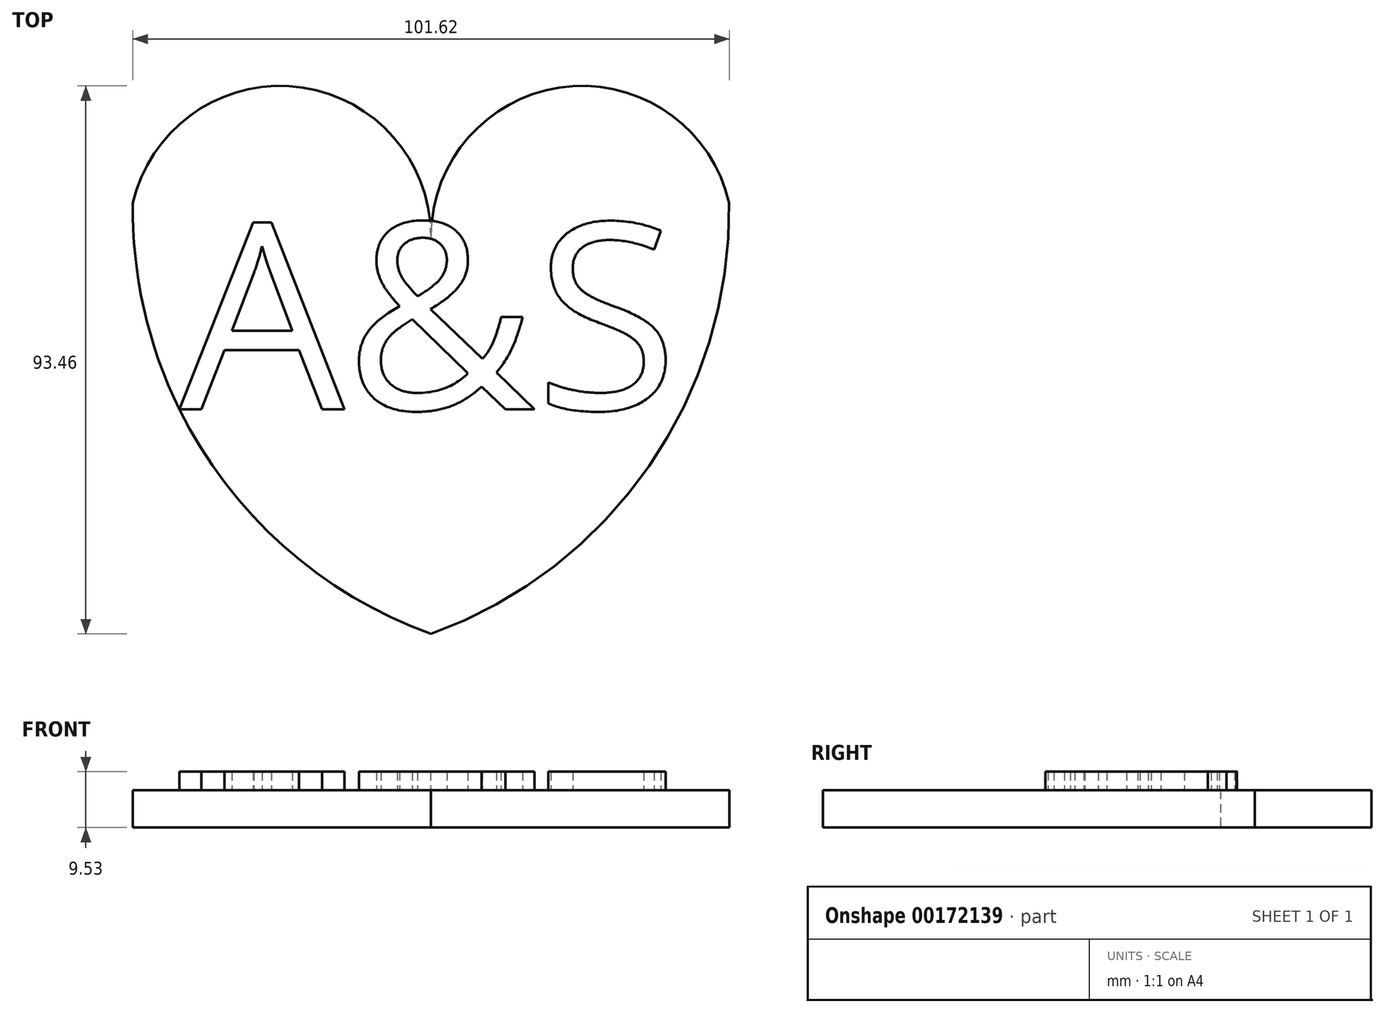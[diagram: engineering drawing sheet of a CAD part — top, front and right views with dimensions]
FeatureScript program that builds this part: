
annotation { "Feature Type Name" : "Feature", "Feature Type Description" : "" }
export const myFeature = defineFeature(function(context is Context, id is Id, definition is map)
    precondition{}
    {
        {
            var Q0;
            Q0=qCreatedBy(makeId("Top.planeOp"),FACE);
            var sketch = newSketch(context, id + "F0", { "sketchPlane" : qUnion([Q0])});
            skLineSegment(sketch, "E0.bottom", {"start": v(-50.8, 50.8) * mm, "end": v(50.8, 50.8) * mm});
            skLineSegment(sketch, "E0.top", {"start": v(-50.8, -50.8) * mm, "end": v(50.8, -50.8) * mm});
            skLineSegment(sketch, "E0.left", {"start": v(-50.8, 50.8) * mm, "end": v(-50.8, -50.8) * mm});
            skLineSegment(sketch, "E0.right", {"start": v(50.8, 50.8) * mm, "end": v(50.8, -50.8) * mm});
            skPoint(sketch, "E0.middle", {"position": v(0, 0) * mm});
            skPoint(sketch, "E1", {"position": v(0, -50.8) * mm});
            skLineSegment(sketch, "E2", {"start": v(0, -50.8) * mm, "end": v(0, 16.93) * mm});
            skArc(sketch, "E3", {"start": v(0, 16.93) * mm, "mid": v(-22.81, 42.5) * mm, "end": v(-50.8, 22.74) * mm});
            skArc(sketch, "E4.MirrorCS", {"start": v(0, 16.93) * mm, "mid": v(22.81, 42.5) * mm, "end": v(50.8, 22.74) * mm});
            skArc(sketch, "E5", {"start": v(-50.8, 22.74) * mm, "mid": v(-37.18, -22.17) * mm, "end": v(0, -50.8) * mm});
            skArc(sketch, "E6.MirrorCS", {"start": v(50.8, 22.74) * mm, "mid": v(37.18, -22.17) * mm, "end": v(0, -50.8) * mm});
            skSolve(sketch);
        }
        {
            var Q0;
            {var subQ0=sQuery(id+"F0.wireOp",EDGE,"E5");var subQ1=sQuery(id+"F0.wireOp",EDGE,"E0.left");var subQ3=makeQuery(id+"F0.imprint","INTERSECT",VERTEX,{"derivedFrom":[subQ1,subQ0]});Q0=makeQuery(id+"F0.imprint","IMPRINT",FACE,{"disambiguationData":[TD([[makeQuery(id+"F0.imprint","IMPRINT",EDGE,{"disambiguationData":[TD([[subQ3,1.0]])],"derivedFrom":subQ1}),-1.0]])]});}
            var Q1;
            {var subQ0=sQuery(id+"F0.wireOp",EDGE,"E6.MirrorCS");var subQ1=sQuery(id+"F0.wireOp",EDGE,"E0.right");var subQ3=makeQuery(id+"F0.imprint","INTERSECT",VERTEX,{"derivedFrom":[subQ1,subQ0]});Q1=makeQuery(id+"F0.imprint","IMPRINT",FACE,{"disambiguationData":[TD([[makeQuery(id+"F0.imprint","IMPRINT",EDGE,{"disambiguationData":[TD([[subQ3,1.0]])],"derivedFrom":subQ1}),1.0]])]});}
            var Q2;
            {var subQ4=sQuery(id+"F0.wireOp",EDGE,"E2");Q2=makeQuery(id+"F0.imprint","IMPRINT",FACE,{"disambiguationData":[TD([[makeQuery(id+"F0.imprint","IMPRINT",EDGE,{"derivedFrom":subQ4}),1.0]])]});}
            var Q3;
            {var subQ4=sQuery(id+"F0.wireOp",EDGE,"E2");Q3=makeQuery(id+"F0.imprint","IMPRINT",FACE,{"disambiguationData":[TD([[makeQuery(id+"F0.imprint","IMPRINT",EDGE,{"derivedFrom":subQ4}),-1.0]])]});}
            extrude(context, id + "F1", {"entities" : qUnion([Q0, Q1, Q2, Q3]), "depth" : 6.35 * mm});
        }
        {
            var Q0;
            Q0=makeQuery(id+"F1.opExtrude","CAP_FACE",FACE,{"disambiguationData":[OSD([sQuery(id+"F0.wireOp",EDGE,"E3"),sQuery(id+"F0.wireOp",EDGE,"E4.MirrorCS"),sQuery(id+"F0.wireOp",EDGE,"E5"),sQuery(id+"F0.wireOp",EDGE,"E6.MirrorCS")])],"isStart":false});
            var sketch = newSketch(context, id + "F2", { "sketchPlane" : qUnion([Q0])});
            skText(sketch, "E7", { "text": "A&S", "fontName": "OpenSans-Regular.ttf"});
            const initialGuessF2  = {"E7": [-0.04286, -0.0125, 1, 0, 0.032]};
            skSetInitialGuess(sketch, initialGuessF2);
            skSolve(sketch);
        }
        {
            var Q0;
            Q0 = qSketchRegion(id + "F2", true);
            extrude(context, id + "F3", {"entities" : qUnion([Q0]), "operationType" : NewBodyOperationType.ADD, "depth" : 3.17 * mm});
        }
    });
